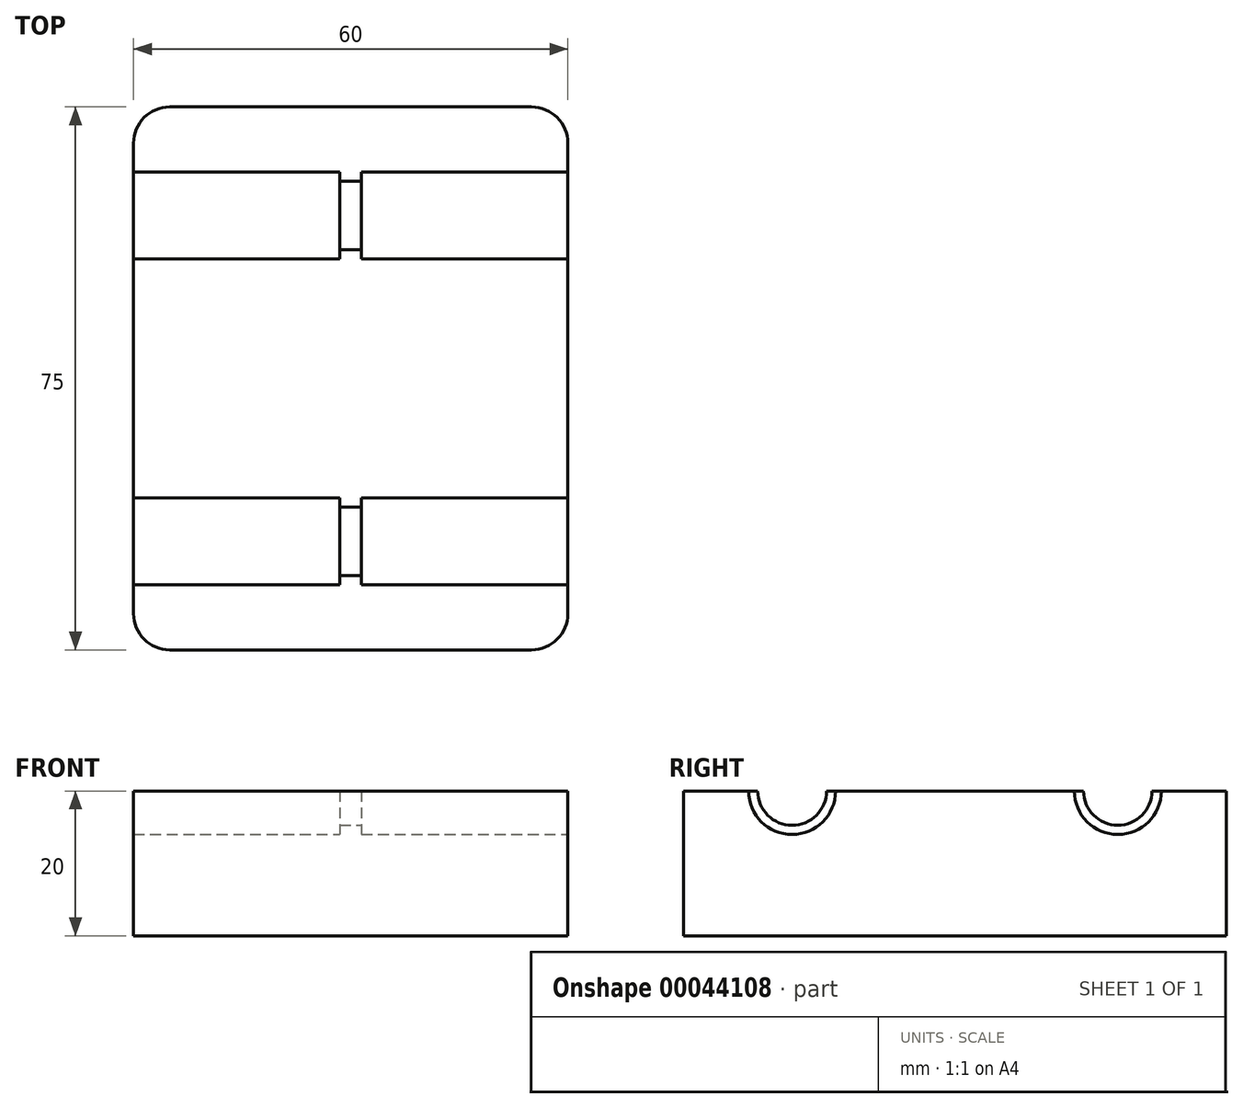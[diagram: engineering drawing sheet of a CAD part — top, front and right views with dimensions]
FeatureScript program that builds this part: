
annotation { "Feature Type Name" : "Feature", "Feature Type Description" : "" }
export const myFeature = defineFeature(function(context is Context, id is Id, definition is map)
    precondition{}
    {
        {
            var Q0;
            Q0=qCreatedBy(makeId("Top.planeOp"),FACE);
            var sketch = newSketch(context, id + "F0", { "sketchPlane" : qUnion([Q0])});
            skLineSegment(sketch, "E0.bottom", {"start": v(-79.44, 75) * mm, "end": v(-29.44, 75) * mm});
            skLineSegment(sketch, "E0.top", {"start": v(-79.44, 0) * mm, "end": v(-29.44, 0) * mm});
            skLineSegment(sketch, "E0.left", {"start": v(-84.44, 70) * mm, "end": v(-84.44, 5) * mm});
            skLineSegment(sketch, "E0.right", {"start": v(-24.44, 70) * mm, "end": v(-24.44, 5) * mm});
            skPoint(sketch, "E1.visualSharp", {"position": v(-84.44, 75) * mm});
            skArc(sketch, "E1.filletArc", {"start": v(-79.44, 75) * mm, "mid": v(-82.97, 73.54) * mm, "end": v(-84.44, 70) * mm});
            skPoint(sketch, "E2.visualSharp", {"position": v(-24.44, 75) * mm});
            skArc(sketch, "E2.filletArc", {"start": v(-24.44, 70) * mm, "mid": v(-25.9, 73.54) * mm, "end": v(-29.44, 75) * mm});
            skPoint(sketch, "E3.visualSharp", {"position": v(-24.44, 0) * mm});
            skArc(sketch, "E3.filletArc", {"start": v(-29.44, 0) * mm, "mid": v(-25.9, 1.46) * mm, "end": v(-24.44, 5) * mm});
            skPoint(sketch, "E4.visualSharp", {"position": v(-84.44, 0) * mm});
            skArc(sketch, "E4.filletArc", {"start": v(-84.44, 5) * mm, "mid": v(-82.97, 1.46) * mm, "end": v(-79.44, 0) * mm});
            skSolve(sketch);
        }
        {
            var Q0;
            Q0 = qSketchRegion(id + "F0", true);
            extrude(context, id + "F1", {"entities" : qUnion([Q0]), "depth" : 20 * mm});
        }
        {
            var Q0;
            Q0=makeQuery(id+"F1.opExtrude","SWEPT_FACE",FACE,{"disambiguationData":[OSD([sQuery(id+"F0.wireOp",EDGE,"E0.right")])]});
            var sketch = newSketch(context, id + "F2", { "sketchPlane" : qUnion([Q0])});
            skLineSegment(sketch, "E5", {"start": v(37.5, 20) * mm, "end": v(60, 20) * mm, "construction": true});
            skLineSegment(sketch, "E6", {"start": v(37.5, 20) * mm, "end": v(15, 20) * mm, "construction": true});
            skLineSegment(sketch, "E7", {"start": v(37.5, 20) * mm, "end": v(37.5, 0) * mm, "construction": true});
            skCircle(sketch, "E8", {"center": v(60, 20) * mm, "radius": 6 * mm});
            skCircle(sketch, "E9", {"center": v(15, 20) * mm, "radius": 6 * mm});
            skSolve(sketch);
        }
        {
            var Q0;
            Q0 = qSketchRegion(id + "F2", true);
            extrude(context, id + "F3", {"entities" : qUnion([Q0]), "operationType" : NewBodyOperationType.REMOVE, "endBound" : BoundingType.THROUGH_ALL, "oppositeDirection" : true, "depth" : 25 * mm});
        }
        {
            var Q0;
            {var subQ0=sQuery(id+"F0.wireOp",EDGE,"E0.left");var subQ1=sQuery(id+"F0.wireOp",EDGE,"E0.right");Q0=makeQuery(id+"F3.boolean.opBoolean","SPLIT",FACE,{"disambiguationData":[TD([makeQuery(id+"F1.opExtrude","SWEPT_FACE",FACE,{"disambiguationData":[OSD([subQ0])]}),makeQuery(id+"F1.opExtrude","SWEPT_FACE",FACE,{"disambiguationData":[OSD([subQ1])]}),makeQuery(id+"F3.opExtrude","SWEPT_FACE",FACE,{"disambiguationData":[OSD([sQuery(id+"F2.wireOp",EDGE,"E8")])]}),makeQuery(id+"F3.opExtrude","SWEPT_FACE",FACE,{"disambiguationData":[OSD([sQuery(id+"F2.wireOp",EDGE,"E9")])]})])],"derivedFrom":makeQuery(id+"F1.opExtrude","CAP_FACE",FACE,{"disambiguationData":[OSD([sQuery(id+"F0.wireOp",EDGE,"E0.bottom"),sQuery(id+"F0.wireOp",EDGE,"E0.top"),subQ0,subQ1,sQuery(id+"F0.wireOp",EDGE,"E1.filletArc"),sQuery(id+"F0.wireOp",EDGE,"E2.filletArc"),sQuery(id+"F0.wireOp",EDGE,"E3.filletArc"),sQuery(id+"F0.wireOp",EDGE,"E4.filletArc")])],"isStart":false})});}
            var sketch = newSketch(context, id + "F4", { "sketchPlane" : qUnion([Q0])});
            skLineSegment(sketch, "E10", {"start": v(-54.44, 54) * mm, "end": v(-54.44, 21.01) * mm, "construction": true});
            skLineSegment(sketch, "E11", {"start": v(-54.44, 54) * mm, "end": v(-52.94, 54) * mm});
            skLineSegment(sketch, "E12", {"start": v(-52.94, 54) * mm, "end": v(-52.94, 66.01) * mm});
            skLineSegment(sketch, "E13", {"start": v(-52.94, 66.01) * mm, "end": v(-55.94, 66.01) * mm});
            skLineSegment(sketch, "E14", {"start": v(-55.94, 66.01) * mm, "end": v(-55.94, 54) * mm});
            skLineSegment(sketch, "E15", {"start": v(-55.94, 54) * mm, "end": v(-54.44, 54) * mm});
            skLineSegment(sketch, "E16", {"start": v(-54.44, 21.01) * mm, "end": v(-52.94, 21.01) * mm});
            skLineSegment(sketch, "E17", {"start": v(-52.94, 21.01) * mm, "end": v(-52.94, 8.83) * mm});
            skLineSegment(sketch, "E18", {"start": v(-52.94, 8.83) * mm, "end": v(-55.94, 8.83) * mm});
            skLineSegment(sketch, "E19", {"start": v(-55.94, 8.83) * mm, "end": v(-55.94, 21.01) * mm});
            skLineSegment(sketch, "E20", {"start": v(-55.94, 21.01) * mm, "end": v(-54.44, 21.01) * mm});
            skSolve(sketch);
        }
        {
            var Q0;
            Q0 = qSketchRegion(id + "F4", true);
            extrude(context, id + "F5", {"entities" : qUnion([Q0]), "operationType" : NewBodyOperationType.ADD, "oppositeDirection" : true, "depth" : 7 * mm});
        }
        {
            var Q0;
            Q0=makeQuery(id+"F1.opExtrude","SWEPT_FACE",FACE,{"disambiguationData":[OSD([sQuery(id+"F0.wireOp",EDGE,"E0.right")])]});
            var sketch = newSketch(context, id + "F6", { "sketchPlane" : qUnion([Q0])});
            skLineSegment(sketch, "E21", {"start": v(37.5, 0) * mm, "end": v(37.5, 20) * mm, "construction": true});
            skLineSegment(sketch, "E22", {"start": v(37.5, 20) * mm, "end": v(60, 20) * mm, "construction": true});
            skLineSegment(sketch, "E23", {"start": v(37.5, 20) * mm, "end": v(15, 20) * mm, "construction": true});
            skCircle(sketch, "E24", {"center": v(60, 20) * mm, "radius": 4.73 * mm});
            skCircle(sketch, "E25", {"center": v(15, 20) * mm, "radius": 4.75 * mm});
            skSolve(sketch);
        }
        {
            var Q0;
            Q0 = qSketchRegion(id + "F6", true);
            extrude(context, id + "F7", {"entities" : qUnion([Q0]), "operationType" : NewBodyOperationType.REMOVE, "endBound" : BoundingType.THROUGH_ALL, "oppositeDirection" : true, "depth" : 25 * mm});
        }
    });
